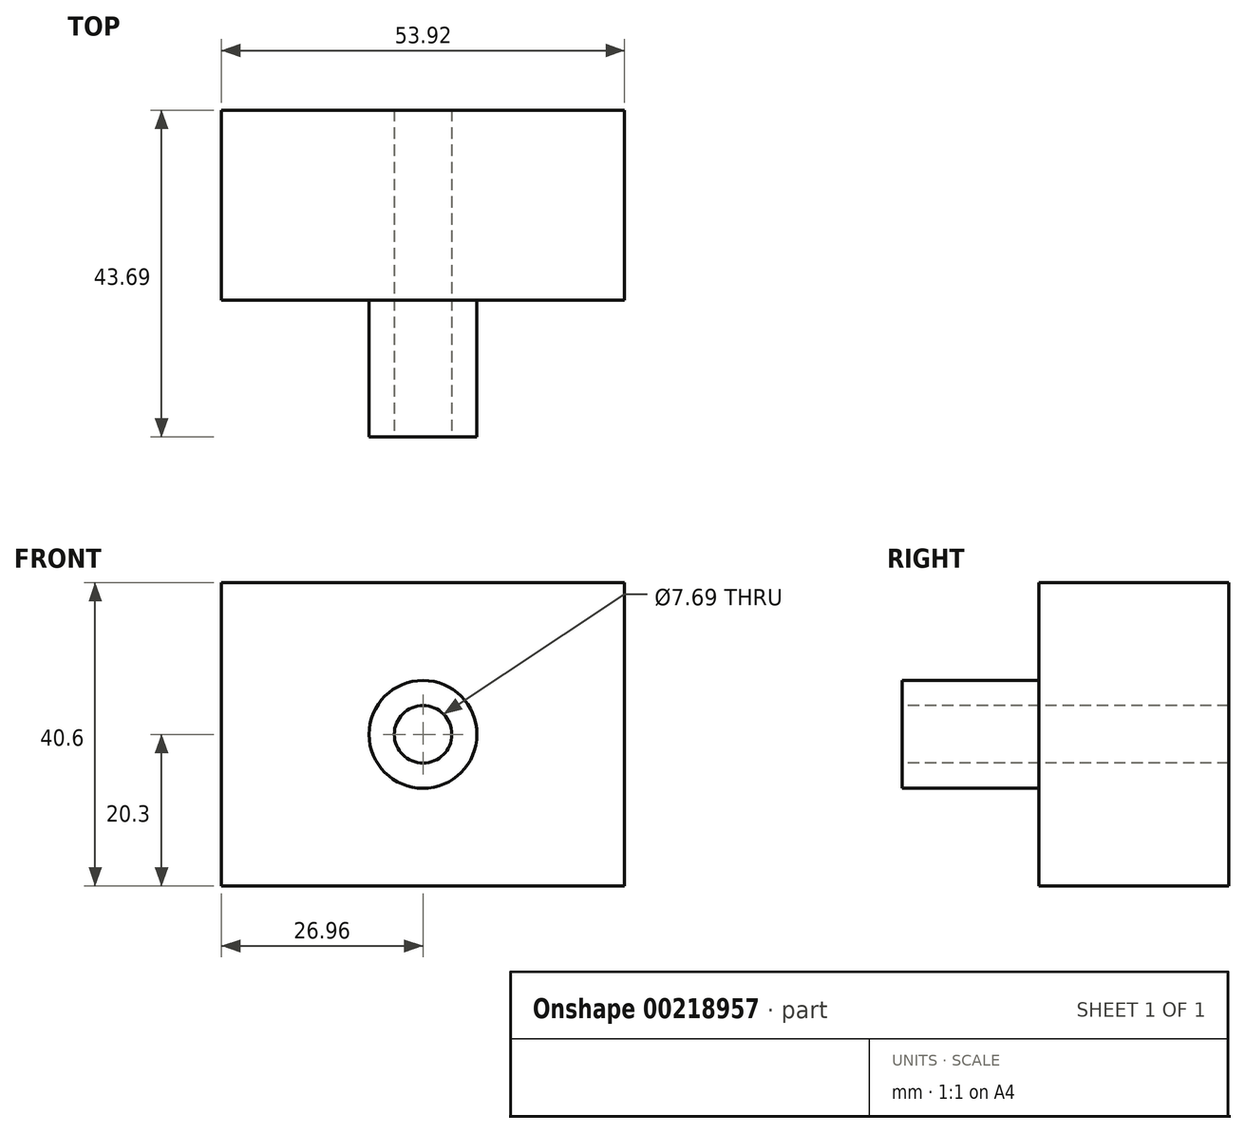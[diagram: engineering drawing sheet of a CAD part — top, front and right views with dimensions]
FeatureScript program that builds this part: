
annotation { "Feature Type Name" : "Feature", "Feature Type Description" : "" }
export const myFeature = defineFeature(function(context is Context, id is Id, definition is map)
    precondition{}
    {
        {
            var Q0;
            Q0=qCreatedBy(makeId("Front.planeOp"),FACE);
            var sketch = newSketch(context, id + "F0", { "sketchPlane" : qUnion([Q0])});
            skLineSegment(sketch, "E0.bottom", {"start": v(26.96, 20.3) * mm, "end": v(-26.96, 20.3) * mm});
            skLineSegment(sketch, "E0.top", {"start": v(26.96, -20.3) * mm, "end": v(-26.96, -20.3) * mm});
            skLineSegment(sketch, "E0.left", {"start": v(26.96, 20.3) * mm, "end": v(26.96, -20.3) * mm});
            skLineSegment(sketch, "E0.right", {"start": v(-26.96, 20.3) * mm, "end": v(-26.96, -20.3) * mm});
            skPoint(sketch, "E0.middle", {"position": v(0, 0) * mm});
            skSolve(sketch);
        }
        {
            var Q0;
            Q0=makeQuery(id+"F0.imprint","IMPRINT",FACE,{"disambiguationData":[TD([[makeQuery(id+"F0.imprint","IMPRINT",EDGE,{"derivedFrom":sQuery(id+"F0.wireOp",EDGE,"E0.bottom")}),1.0]])]});
            extrude(context, id + "F1", {"entities" : qUnion([Q0]), "depth" : 25.4 * mm});
        }
        {
            var Q0;
            Q0=makeQuery(id+"F1.opExtrude","CAP_FACE",FACE,{"disambiguationData":[OSD([sQuery(id+"F0.wireOp",EDGE,"E0.bottom"),sQuery(id+"F0.wireOp",EDGE,"E0.top"),sQuery(id+"F0.wireOp",EDGE,"E0.left"),sQuery(id+"F0.wireOp",EDGE,"E0.right")])],"isStart":false});
            var sketch = newSketch(context, id + "F2", { "sketchPlane" : qUnion([Q0])});
            skCircle(sketch, "E1", {"center": v(0, 0) * mm, "radius": 7.21 * mm});
            skSolve(sketch);
        }
        {
            var Q0;
            Q0=makeQuery(id+"F2.imprint","IMPRINT",FACE,{"disambiguationData":[TD([[makeQuery(id+"F2.imprint","IMPRINT",EDGE,{"derivedFrom":sQuery(id+"F2.wireOp",EDGE,"E1")}),1.0]])]});
            extrude(context, id + "F3", {"entities" : qUnion([Q0]), "operationType" : NewBodyOperationType.ADD, "depth" : 18.29 * mm});
        }
        {
            var Q0;
            Q0=makeQuery(id+"F3.opExtrude","CAP_FACE",FACE,{"disambiguationData":[OSD([sQuery(id+"F2.wireOp",EDGE,"E1")])],"isStart":false});
            var sketch = newSketch(context, id + "F4", { "sketchPlane" : qUnion([Q0])});
            skCircle(sketch, "E2", {"center": v(0, 0) * mm, "radius": 3.85 * mm});
            skSolve(sketch);
        }
        {
            var Q0;
            Q0=makeQuery(id+"F4.imprint","IMPRINT",FACE,{"disambiguationData":[TD([[makeQuery(id+"F4.imprint","IMPRINT",EDGE,{"derivedFrom":sQuery(id+"F4.wireOp",EDGE,"E2")}),1.0]])]});
            extrude(context, id + "F5", {"entities" : qUnion([Q0]), "operationType" : NewBodyOperationType.REMOVE, "endBound" : BoundingType.THROUGH_ALL, "oppositeDirection" : true, "depth" : 25.4 * mm});
        }
    });
